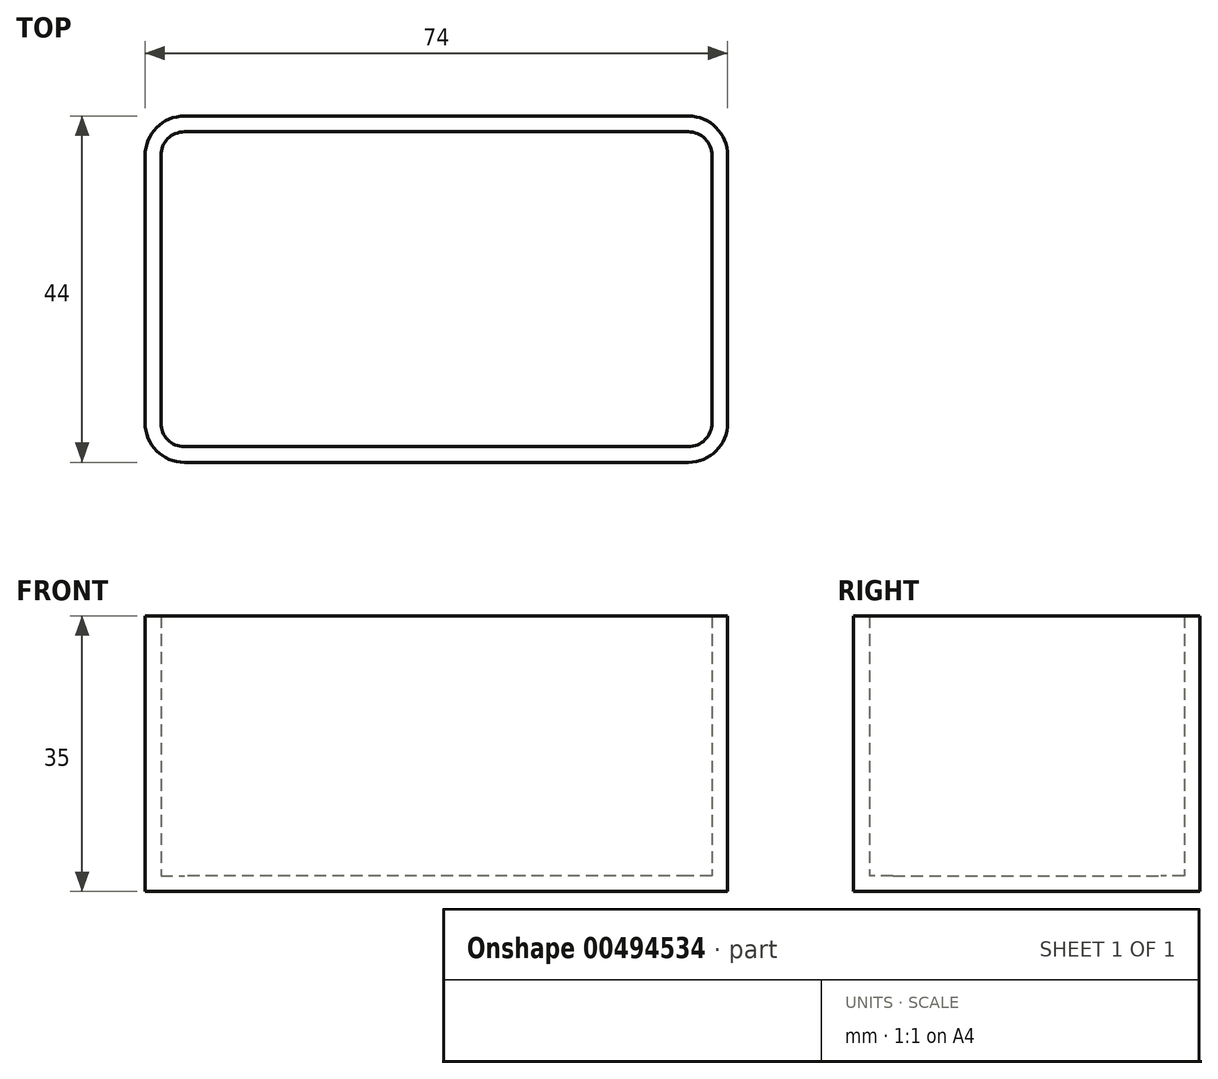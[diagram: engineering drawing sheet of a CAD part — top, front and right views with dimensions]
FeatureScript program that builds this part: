
annotation { "Feature Type Name" : "Feature", "Feature Type Description" : "" }
export const myFeature = defineFeature(function(context is Context, id is Id, definition is map)
    precondition{}
    {
        {
            var Q0;
            Q0=qCreatedBy(makeId("Top.planeOp"),FACE);
            var sketch = newSketch(context, id + "F0", { "sketchPlane" : qUnion([Q0])});
            skLineSegment(sketch, "E0.bottom", {"start": v(32, -20) * mm, "end": v(-32, -20) * mm});
            skLineSegment(sketch, "E0.top", {"start": v(32, 20) * mm, "end": v(-32, 20) * mm});
            skLineSegment(sketch, "E0.left", {"start": v(35, -17) * mm, "end": v(35, 17) * mm});
            skLineSegment(sketch, "E0.right", {"start": v(-35, -17) * mm, "end": v(-35, 17) * mm});
            skPoint(sketch, "E0.middle", {"position": v(0, 0) * mm});
            skPoint(sketch, "E1.visualSharp", {"position": v(-35, 20) * mm});
            skArc(sketch, "E1.filletArc", {"start": v(-32, 20) * mm, "mid": v(-34.12, 19.12) * mm, "end": v(-35, 17) * mm});
            skPoint(sketch, "E2.visualSharp", {"position": v(-35, -20) * mm});
            skArc(sketch, "E2.filletArc", {"start": v(-35, -17) * mm, "mid": v(-34.12, -19.12) * mm, "end": v(-32, -20) * mm});
            skPoint(sketch, "E3.visualSharp", {"position": v(35, -20) * mm});
            skArc(sketch, "E3.filletArc", {"start": v(32, -20) * mm, "mid": v(34.12, -19.12) * mm, "end": v(35, -17) * mm});
            skPoint(sketch, "E4.visualSharp", {"position": v(35, 20) * mm});
            skArc(sketch, "E4.filletArc", {"start": v(35, 17) * mm, "mid": v(34.12, 19.12) * mm, "end": v(32, 20) * mm});
            skArc(sketch, "E5.0", {"start": v(37, 17) * mm, "mid": v(35.54, 20.54) * mm, "end": v(32, 22) * mm});
            skLineSegment(sketch, "E5.1", {"start": v(37, -17) * mm, "end": v(37, 17) * mm});
            skLineSegment(sketch, "E5.2", {"start": v(32, 22) * mm, "end": v(-32, 22) * mm});
            skArc(sketch, "E5.3", {"start": v(32, -22) * mm, "mid": v(35.54, -20.54) * mm, "end": v(37, -17) * mm});
            skArc(sketch, "E5.4", {"start": v(-32, 22) * mm, "mid": v(-35.54, 20.54) * mm, "end": v(-37, 17) * mm});
            skLineSegment(sketch, "E5.5", {"start": v(-37, -17) * mm, "end": v(-37, 17) * mm});
            skArc(sketch, "E5.6", {"start": v(-37, -17) * mm, "mid": v(-35.54, -20.54) * mm, "end": v(-32, -22) * mm});
            skLineSegment(sketch, "E5.7", {"start": v(32, -22) * mm, "end": v(-32, -22) * mm});
            skSolve(sketch);
        }
        {
            var Q0;
            Q0=makeQuery(id+"F0.imprint","IMPRINT",FACE,{"disambiguationData":[TD([[makeQuery(id+"F0.imprint","IMPRINT",EDGE,{"derivedFrom":sQuery(id+"F0.wireOp",EDGE,"E0.bottom")}),-1.0]])]});
            extrude(context, id + "F1", {"entities" : qUnion([Q0]), "depth" : 2 * mm});
        }
        {
            var Q0;
            Q0 = qSketchRegion(id + "F0", true);
            extrude(context, id + "F2", {"entities" : qUnion([Q0]), "operationType" : NewBodyOperationType.ADD, "depth" : 35 * mm});
        }
    });
